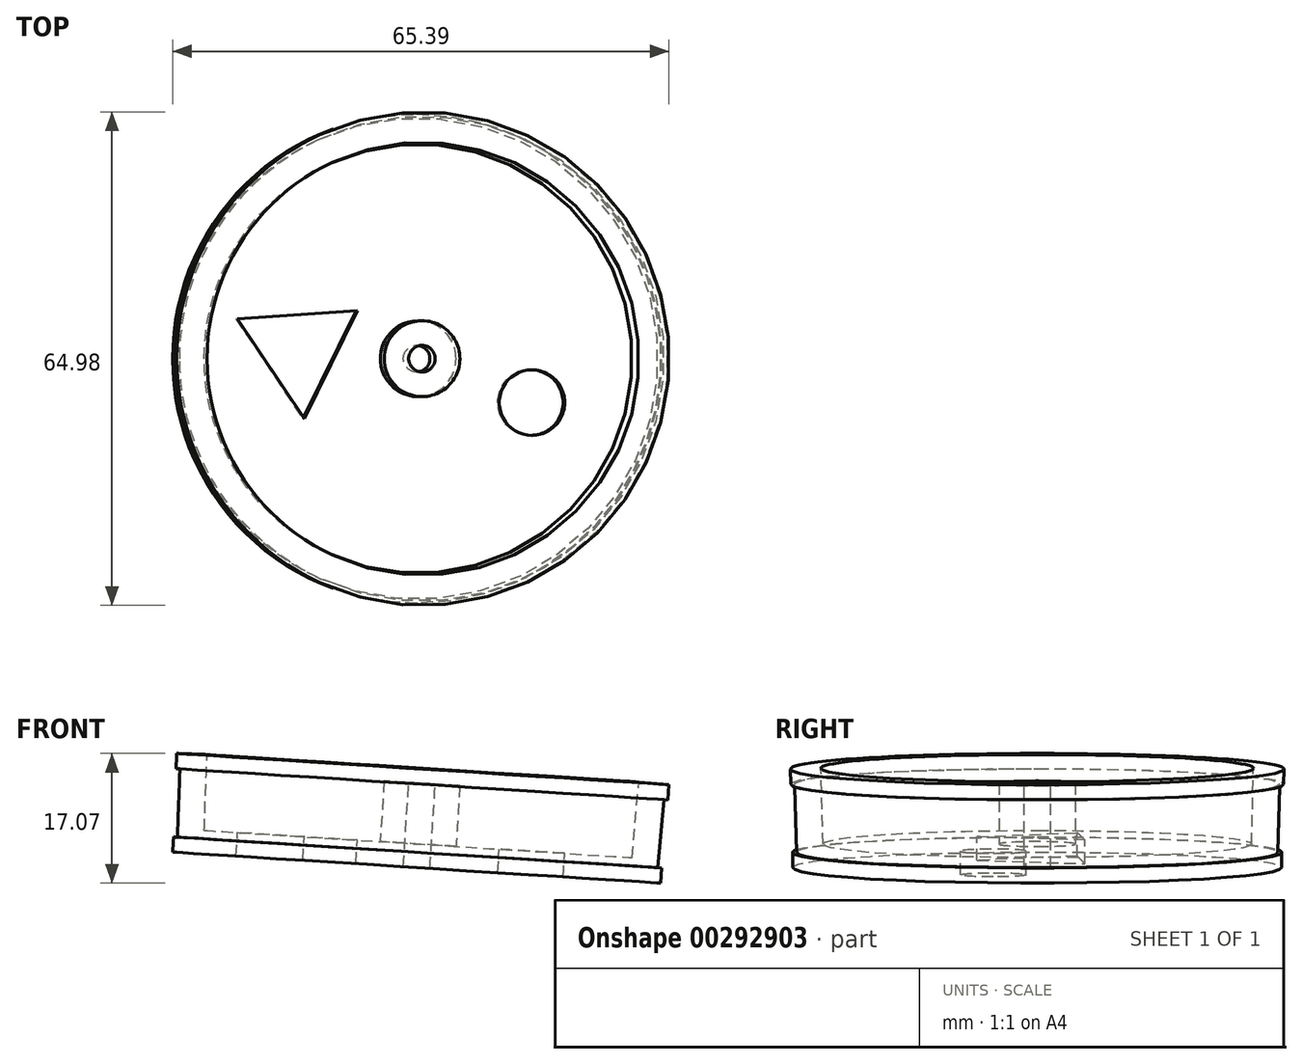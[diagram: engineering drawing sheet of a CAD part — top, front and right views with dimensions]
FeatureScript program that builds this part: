
annotation { "Feature Type Name" : "Feature", "Feature Type Description" : "" }
export const myFeature = defineFeature(function(context is Context, id is Id, definition is map)
    precondition{}
    {
        {
            var Q0;
            Q0=qCreatedBy(makeId("Front.planeOp"),FACE);
            var sketch = newSketch(context, id + "F0", { "sketchPlane" : qUnion([Q0])});
            skLineSegment(sketch, "E0", {"start": v(0, 0) * mm, "end": v(32.14, -2.04) * mm});
            skLineSegment(sketch, "E1", {"start": v(32.14, -2.04) * mm, "end": v(32.26, -0.04) * mm});
            skLineSegment(sketch, "E2", {"start": v(32.26, -0.04) * mm, "end": v(31.76, 0) * mm});
            skLineSegment(sketch, "E3", {"start": v(31.76, 0) * mm, "end": v(32.57, 8.96) * mm});
            skLineSegment(sketch, "E4", {"start": v(32.57, 8.96) * mm, "end": v(33.07, 8.92) * mm});
            skLineSegment(sketch, "E5", {"start": v(33.07, 8.92) * mm, "end": v(33.25, 10.91) * mm});
            skLineSegment(sketch, "E6", {"start": v(33.25, 10.91) * mm, "end": v(29.27, 11.27) * mm});
            skLineSegment(sketch, "E7", {"start": v(29.27, 11.27) * mm, "end": v(28.37, 1.31) * mm});
            skLineSegment(sketch, "E8", {"start": v(28.37, 1.31) * mm, "end": v(0.2, 3.1) * mm});
            skLineSegment(sketch, "E9", {"start": v(0, 0) * mm, "end": v(0.2, 3.1) * mm});
            skPoint(sketch, "E10.orphan", {"position": v(0.05, 3.1) * mm});
            skSolve(sketch);
        }
        {
            var Q0;
            Q0 = qSketchRegion(id + "F0", true);
            var Q1;
            Q1=sQuery(id+"F0.wireOp",EDGE,"E9");
            revolve(context, id + "F1", {"entities" : qUnion([Q0]), "axis" : qUnion([Q1]), "revolveType" : RevolveType.FULL});
        }
        {
            var Q0;
            Q0=makeQuery(id+"F1.opRevolve","SWEPT_FACE",FACE,{"disambiguationData":[OSD([sQuery(id+"F0.wireOp",EDGE,"E8")])]});
            var sketch = newSketch(context, id + "F2", { "sketchPlane" : qUnion([Q0])});
            skCircle(sketch, "E11.0", {"center": v(0, 0) * mm, "radius": 28.23 * mm});
            skCircle(sketch, "E12", {"center": v(0, 0) * mm, "radius": 5 * mm});
            skSolve(sketch);
        }
        {
            var Q0;
            Q0=makeQuery(id+"F2.imprint","IMPRINT",FACE,{"disambiguationData":[TD([[makeQuery(id+"F2.imprint","IMPRINT",EDGE,{"derivedFrom":sQuery(id+"F2.wireOp",EDGE,"E12")}),1.0]])]});
            extrude(context, id + "F3", {"entities" : qUnion([Q0]), "operationType" : NewBodyOperationType.ADD, "depth" : 8 * mm});
        }
        {
            var Q0;
            Q0=makeQuery(id+"F3.opExtrude","CAP_FACE",FACE,{"disambiguationData":[OSD([sQuery(id+"F2.wireOp",EDGE,"E12")])],"isStart":false});
            var sketch = newSketch(context, id + "F4", { "sketchPlane" : qUnion([Q0])});
            skCircle(sketch, "E13.0.0", {"center": v(0, 0) * mm, "radius": 5 * mm});
            skCircle(sketch, "E14", {"center": v(0, 0) * mm, "radius": 1.75 * mm});
            skSolve(sketch);
        }
        {
            var Q0;
            Q0=makeQuery(id+"F4.imprint","IMPRINT",FACE,{"disambiguationData":[TD([[makeQuery(id+"F4.imprint","IMPRINT",EDGE,{"derivedFrom":sQuery(id+"F4.wireOp",EDGE,"E14")}),1.0]])]});
            extrude(context, id + "F5", {"entities" : qUnion([Q0]), "operationType" : NewBodyOperationType.REMOVE, "oppositeDirection" : true, "depth" : 40 * mm});
        }
        {
            var Q0;
            Q0=makeQuery(id+"F1.opRevolve","SWEPT_FACE",FACE,{"disambiguationData":[OSD([sQuery(id+"F0.wireOp",EDGE,"E8")])]});
            var sketch = newSketch(context, id + "F6", { "sketchPlane" : qUnion([Q0])});
            skCircle(sketch, "E15", {"center": v(15.02, -5.78) * mm, "radius": 4.32 * mm});
            skCircle(sketch, "E16.cCircle", {"center": v(-15.62, 1.2) * mm, "radius": 4.57 * mm, "construction": true});
            skLineSegment(sketch, "E16.0", {"start": v(-15.02, -7.92) * mm, "end": v(-23.83, 5.25) * mm});
            skLineSegment(sketch, "E16.1", {"start": v(-23.83, 5.25) * mm, "end": v(-8.02, 6.3) * mm});
            skLineSegment(sketch, "E16.2", {"start": v(-8.02, 6.3) * mm, "end": v(-15.02, -7.92) * mm});
            skPoint(sketch, "E16.0.midPoint", {"position": v(-19.42, -1.33) * mm});
            skSolve(sketch);
        }
        {
            var Q0;
            Q0=makeQuery(id+"F6.imprint","IMPRINT",FACE,{"disambiguationData":[TD([[makeQuery(id+"F6.imprint","IMPRINT",EDGE,{"derivedFrom":sQuery(id+"F6.wireOp",EDGE,"E16.0")}),-1.0]])]});
            var Q1;
            Q1=makeQuery(id+"F6.imprint","IMPRINT",FACE,{"disambiguationData":[TD([[makeQuery(id+"F6.imprint","IMPRINT",EDGE,{"derivedFrom":sQuery(id+"F6.wireOp",EDGE,"E15")}),1.0]])]});
            extrude(context, id + "F7", {"entities" : qUnion([Q0, Q1]), "operationType" : NewBodyOperationType.REMOVE, "oppositeDirection" : true, "depth" : 25 * mm});
        }
    });
